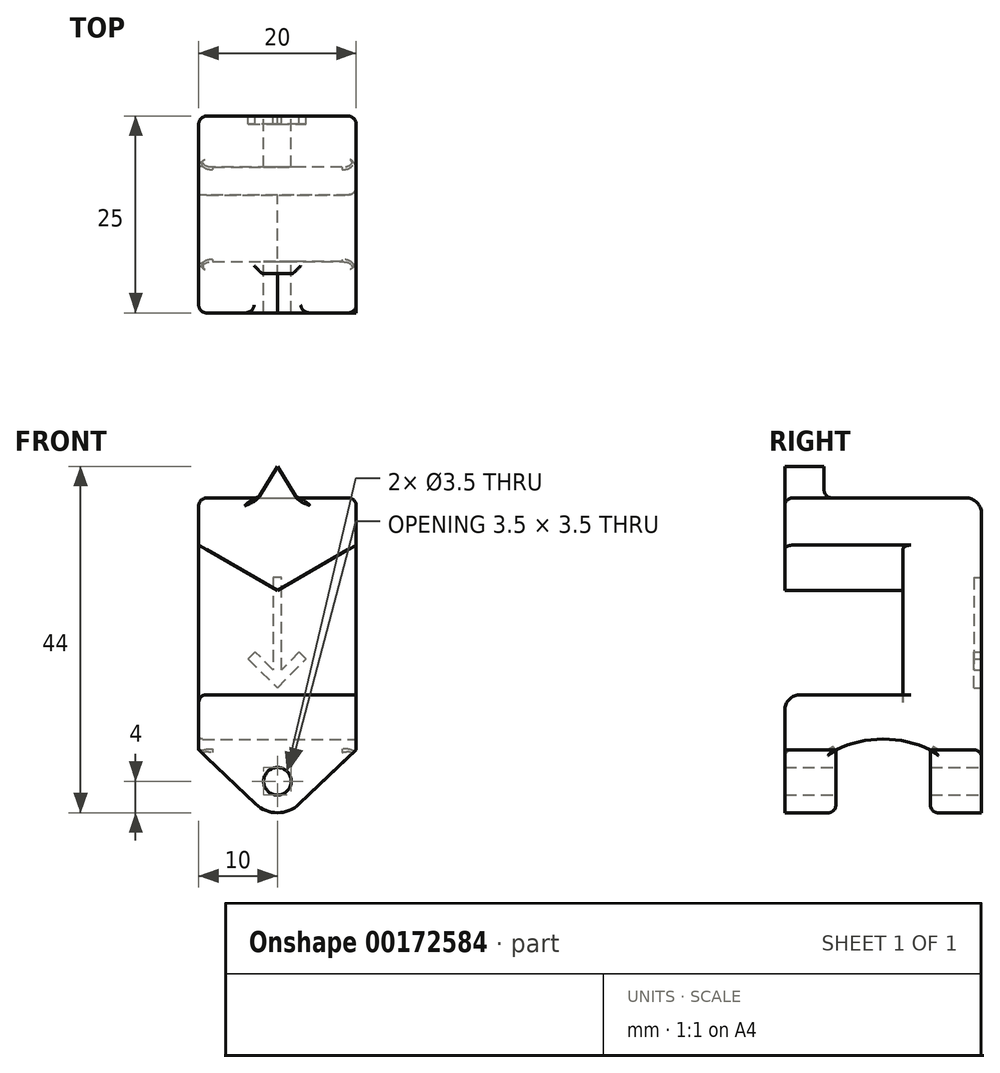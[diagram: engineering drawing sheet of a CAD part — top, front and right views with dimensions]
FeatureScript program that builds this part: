
annotation { "Feature Type Name" : "Feature", "Feature Type Description" : "" }
export const myFeature = defineFeature(function(context is Context, id is Id, definition is map)
    precondition{}
    {
        {
            var Q0;
            Q0=qCreatedBy(makeId("Front.planeOp"),FACE);
            var sketch = newSketch(context, id + "F0", { "sketchPlane" : qUnion([Q0])});
            skLineSegment(sketch, "E0.bottom", {"start": v(0, 0) * mm, "end": v(20, 0) * mm});
            skLineSegment(sketch, "E0.top", {"start": v(0, 40) * mm, "end": v(20, 40) * mm});
            skLineSegment(sketch, "E0.left", {"start": v(0, 0) * mm, "end": v(0, 40) * mm});
            skLineSegment(sketch, "E0.right", {"start": v(20, 0) * mm, "end": v(20, 40) * mm});
            skSolve(sketch);
        }
        {
            var Q0;
            Q0 = qSketchRegion(id + "F0", true);
            extrude(context, id + "F1", {"entities" : qUnion([Q0]), "depth" : 10 * mm});
        }
        {
            var Q0;
            Q0=makeQuery(id+"F1.opExtrude","CAP_FACE",FACE,{"disambiguationData":[OSD([sQuery(id+"F0.wireOp",EDGE,"E0.bottom"),sQuery(id+"F0.wireOp",EDGE,"E0.top"),sQuery(id+"F0.wireOp",EDGE,"E0.left"),sQuery(id+"F0.wireOp",EDGE,"E0.right")])],"isStart":false});
            var sketch = newSketch(context, id + "F2", { "sketchPlane" : qUnion([Q0])});
            skLineSegment(sketch, "E1", {"start": v(0, 40) * mm, "end": v(20, 40) * mm});
            skLineSegment(sketch, "E2", {"start": v(20, 40) * mm, "end": v(20, 34) * mm});
            skLineSegment(sketch, "E3", {"start": v(20, 34) * mm, "end": v(10, 28.23) * mm});
            skPoint(sketch, "E3.endSnap0", {"position": v(10, 40) * mm});
            skLineSegment(sketch, "E4", {"start": v(10, 28.23) * mm, "end": v(0, 34) * mm});
            skLineSegment(sketch, "E5", {"start": v(0, 34) * mm, "end": v(0, 40) * mm});
            skLineSegment(sketch, "E6.bottom", {"start": v(0, 0) * mm, "end": v(20, 0) * mm});
            skLineSegment(sketch, "E6.top", {"start": v(0, 15) * mm, "end": v(20, 15) * mm});
            skLineSegment(sketch, "E6.left", {"start": v(0, 0) * mm, "end": v(0, 15) * mm});
            skLineSegment(sketch, "E6.right", {"start": v(20, 0) * mm, "end": v(20, 15) * mm});
            skSolve(sketch);
        }
        {
            var Q0;
            Q0 = qSketchRegion(id + "F2", true);
            extrude(context, id + "F3", {"entities" : qUnion([Q0]), "operationType" : NewBodyOperationType.ADD, "depth" : 15 * mm});
        }
        {
            var Q0;
            Q0=makeQuery(id+"F3.boolean.opBoolean","MERGE",FACE,{"derivedFrom":[makeQuery(id+"F1.opExtrude","SWEPT_FACE",FACE,{"disambiguationData":[OSD([sQuery(id+"F0.wireOp",EDGE,"E0.right")])]}),makeQuery(id+"F3.opExtrude","SWEPT_FACE",FACE,{"disambiguationData":[OSD([sQuery(id+"F2.wireOp",EDGE,"E2")])]}),makeQuery(id+"F3.opExtrude","SWEPT_FACE",FACE,{"disambiguationData":[OSD([sQuery(id+"F2.wireOp",EDGE,"E6.right")])]})]});
            var sketch = newSketch(context, id + "F4", { "sketchPlane" : qUnion([Q0])});
            skLineSegment(sketch, "E7.bottom", {"start": v(-18.5, 0) * mm, "end": v(-6.5, 0) * mm});
            skLineSegment(sketch, "E7.top", {"start": v(-18.5, 8) * mm, "end": v(-6.5, 8) * mm});
            skLineSegment(sketch, "E7.left", {"start": v(-18.5, 0) * mm, "end": v(-18.5, 8) * mm});
            skLineSegment(sketch, "E7.right", {"start": v(-6.5, 0) * mm, "end": v(-6.5, 8) * mm});
            skArc(sketch, "E8", {"start": v(-6.5, 8) * mm, "mid": v(-12.5, 9.35) * mm, "end": v(-18.5, 8) * mm});
            skSolve(sketch);
        }
        {
            var Q0;
            Q0 = qSketchRegion(id + "F4", true);
            extrude(context, id + "F5", {"entities" : qUnion([Q0]), "operationType" : NewBodyOperationType.REMOVE, "oppositeDirection" : true, "depth" : 25 * mm});
        }
        {
            var Q0;
            Q0=makeQuery(id+"F5.boolean.opBoolean","COPY",FACE,{"derivedFrom":makeQuery(id+"F5.opExtrude","SWEPT_FACE",FACE,{"disambiguationData":[OSD([sQuery(id+"F4.wireOp",EDGE,"E7.left")])]})});
            var sketch = newSketch(context, id + "F6", { "sketchPlane" : qUnion([Q0])});
            skCircle(sketch, "E9", {"center": v(-10, 4) * mm, "radius": 1.75 * mm});
            skPoint(sketch, "E9.centerSnap0", {"position": v(-20, 4) * mm});
            skPoint(sketch, "E9.centerSnap1", {"position": v(-10, 0) * mm});
            skSolve(sketch);
        }
        {
            var Q0;
            Q0 = qSketchRegion(id + "F6", true);
            extrude(context, id + "F7", {"entities" : qUnion([Q0]), "operationType" : NewBodyOperationType.REMOVE, "oppositeDirection" : true, "depth" : 25 * mm, "hasSecondDirection" : true, "secondDirectionOppositeDirection" : false, "secondDirectionDepth" : 25 * mm});
        }
        {
            var Q0;
            Q0=makeQuery(id+"F3.opExtrude","CAP_FACE",FACE,{"disambiguationData":[OSD([sQuery(id+"F2.wireOp",EDGE,"E6.bottom"),sQuery(id+"F2.wireOp",EDGE,"E6.top"),sQuery(id+"F2.wireOp",EDGE,"E6.left"),sQuery(id+"F2.wireOp",EDGE,"E6.right")])],"isStart":false});
            var sketch = newSketch(context, id + "F8", { "sketchPlane" : qUnion([Q0])});
            skArc(sketch, "E10", {"start": v(10, 0) * mm, "mid": v(11.49, 0.29) * mm, "end": v(12.76, 1.1) * mm});
            skLineSegment(sketch, "E11", {"start": v(12.76, 1.1) * mm, "end": v(20, 8) * mm});
            skLineSegment(sketch, "E12", {"start": v(10, 4) * mm, "end": v(10, 0) * mm, "construction": true});
            skLineSegment(sketch, "E13.MirrorCS", {"start": v(7.24, 1.1) * mm, "end": v(0, 8) * mm});
            skArc(sketch, "E14.MirrorCS", {"start": v(10, 0) * mm, "mid": v(8.51, 0.29) * mm, "end": v(7.24, 1.1) * mm});
            skSolve(sketch);
        }
        {
            var Q0;
            {var subQ0=sQuery(id+"F8.wireOp",EDGE,"E10");Q0=makeQuery(id+"F8.imprint","IMPRINT",FACE,{"disambiguationData":[TD([[makeQuery(id+"F8.imprint","IMPRINT",EDGE,{"derivedFrom":subQ0}),-1.0]])]});}
            var Q1;
            {var subQ0=sQuery(id+"F8.wireOp",EDGE,"E13.MirrorCS");Q1=makeQuery(id+"F8.imprint","IMPRINT",FACE,{"disambiguationData":[TD([[makeQuery(id+"F8.imprint","IMPRINT",EDGE,{"derivedFrom":subQ0}),1.0]])]});}
            extrude(context, id + "F9", {"entities" : qUnion([Q0, Q1]), "operationType" : NewBodyOperationType.REMOVE, "oppositeDirection" : true, "depth" : 25 * mm});
        }
        {
            var Q0;
            Q0=makeQuery(id+"F1.opExtrude","CAP_EDGE",EDGE,{"disambiguationData":[OSD([sQuery(id+"F0.wireOp",EDGE,"E0.top")])],"isStart":true});
            var Q1;
            Q1=makeQuery(id+"F3.opExtrude","CAP_EDGE",EDGE,{"disambiguationData":[OSD([sQuery(id+"F2.wireOp",EDGE,"E6.top")])],"isStart":true});
            var Q2;
            Q2=makeQuery(id+"F3.opExtrude","CAP_EDGE",EDGE,{"disambiguationData":[OSD([sQuery(id+"F2.wireOp",EDGE,"E6.top")])],"isStart":false});
            fillet(context, id + "F10", {"entities" : qUnion([Q0, Q1, Q2]), "radius" : 2 * mm, "tangentPropagation" : true, "allowEdgeOverflow" : false});
        }
        {
            var Q0;
            Q0=makeQuery(id+"F1.opExtrude","CAP_EDGE",EDGE,{"disambiguationData":[OSD([sQuery(id+"F0.wireOp",EDGE,"E0.left")])],"isStart":true});
            var Q1;
            Q1=makeQuery(id+"F1.opExtrude","CAP_EDGE",EDGE,{"disambiguationData":[OSD([sQuery(id+"F0.wireOp",EDGE,"E0.right")])],"isStart":true});
            var Q2;
            Q2=makeQuery(id+"F9.boolean.opBoolean","COPY",EDGE,{"derivedFrom":makeQuery(id+"F9.opExtrude","CAP_EDGE",EDGE,{"disambiguationData":[OSD([sQuery(id+"F8.wireOp",EDGE,"E13.MirrorCS")])],"isStart":false})});
            var Q3;
            Q3=makeQuery(id+"F9.boolean.opBoolean","COPY",EDGE,{"derivedFrom":makeQuery(id+"F9.opExtrude","CAP_EDGE",EDGE,{"disambiguationData":[OSD([sQuery(id+"F8.wireOp",EDGE,"E13.MirrorCS")])],"isStart":true})});
            var Q4;
            Q4=makeQuery(id+"F9.boolean.opBoolean","INTERSECT",EDGE,{"derivedFrom":[makeQuery(id+"F5.boolean.opBoolean","COPY",FACE,{"derivedFrom":makeQuery(id+"F5.opExtrude","SWEPT_FACE",FACE,{"disambiguationData":[OSD([sQuery(id+"F4.wireOp",EDGE,"E7.right")])]})}),makeQuery(id+"F9.opExtrude","SWEPT_FACE",FACE,{"disambiguationData":[OSD([sQuery(id+"F8.wireOp",EDGE,"E13.MirrorCS")])]})]});
            var Q5;
            Q5=makeQuery(id+"F9.boolean.opBoolean","INTERSECT",EDGE,{"derivedFrom":[makeQuery(id+"F5.boolean.opBoolean","COPY",FACE,{"derivedFrom":makeQuery(id+"F5.opExtrude","SWEPT_FACE",FACE,{"disambiguationData":[OSD([sQuery(id+"F4.wireOp",EDGE,"E7.left")])]})}),makeQuery(id+"F9.opExtrude","SWEPT_FACE",FACE,{"disambiguationData":[OSD([sQuery(id+"F8.wireOp",EDGE,"E13.MirrorCS")])]})]});
            var Q6;
            Q6=makeQuery(id+"F3.opExtrude","SWEPT_EDGE",EDGE,{"disambiguationData":[OSD([sQuery(id+"F0.wireOp",EDGE,"E0.left"),sQuery(id+"F2.wireOp",EDGE,"E6.top"),sQuery(id+"F2.wireOp",EDGE,"E6.left")])]});
            var Q7;
            Q7=makeQuery(id+"F1.opExtrude","CAP_EDGE",EDGE,{"disambiguationData":[OSD([sQuery(id+"F0.wireOp",EDGE,"E0.right")])],"isStart":false});
            var Q8;
            Q8=makeQuery(id+"F3.opExtrude","CAP_EDGE",EDGE,{"disambiguationData":[OSD([sQuery(id+"F2.wireOp",EDGE,"E5")])],"isStart":false});
            var Q9;
            Q9=makeQuery(id+"F3.opExtrude","CAP_EDGE",EDGE,{"disambiguationData":[OSD([sQuery(id+"F2.wireOp",EDGE,"E1")])],"isStart":false});
            var Q10;
            Q10=makeQuery(id+"F3.opExtrude","CAP_EDGE",EDGE,{"disambiguationData":[OSD([sQuery(id+"F2.wireOp",EDGE,"E2")])],"isStart":false});
            fillet(context, id + "F11", {"entities" : qUnion([Q0, Q1, Q2, Q3, Q4, Q5, Q6, Q7, Q8, Q9, Q10]), "radius" : 1 * mm, "tangentPropagation" : true, "allowEdgeOverflow" : false});
        }
        {
            var Q0;
            Q0=makeQuery(id+"F5.boolean.opBoolean","COPY",EDGE,{"derivedFrom":makeQuery(id+"F5.opExtrude","SWEPT_EDGE",EDGE,{"disambiguationData":[OSD([sQuery(id+"F4.wireOp",EDGE,"E7.top"),sQuery(id+"F4.wireOp",EDGE,"E7.right")])]})});
            var Q1;
            Q1=makeQuery(id+"F5.boolean.opBoolean","COPY",EDGE,{"derivedFrom":makeQuery(id+"F5.opExtrude","SWEPT_EDGE",EDGE,{"disambiguationData":[OSD([sQuery(id+"F4.wireOp",EDGE,"E7.top"),sQuery(id+"F4.wireOp",EDGE,"E7.left")])]})});
            fillet(context, id + "F12", {"entities" : qUnion([Q0, Q1]), "radius" : 0.5 * mm, "tangentPropagation" : true, "allowEdgeOverflow" : false});
        }
        {
            var Q0;
            Q0=makeQuery(id+"F1.opExtrude","CAP_FACE",FACE,{"disambiguationData":[OSD([sQuery(id+"F0.wireOp",EDGE,"E0.bottom"),sQuery(id+"F0.wireOp",EDGE,"E0.top"),sQuery(id+"F0.wireOp",EDGE,"E0.left"),sQuery(id+"F0.wireOp",EDGE,"E0.right")])],"isStart":true});
            var sketch = newSketch(context, id + "F13", { "sketchPlane" : qUnion([Q0])});
            skLineSegment(sketch, "E15", {"start": v(-9.46, 29.87) * mm, "end": v(-9.46, 18.15) * mm});
            skLineSegment(sketch, "E16", {"start": v(-9.46, 18.15) * mm, "end": v(-7.17, 20.42) * mm});
            skLineSegment(sketch, "E17", {"start": v(-7.17, 20.42) * mm, "end": v(-6.3, 19.54) * mm});
            skLineSegment(sketch, "E18", {"start": v(-6.3, 19.54) * mm, "end": v(-10, 15.87) * mm});
            skLineSegment(sketch, "E19", {"start": v(-10, 15.87) * mm, "end": v(-13.65, 19.54) * mm});
            skLineSegment(sketch, "E20", {"start": v(-13.65, 19.54) * mm, "end": v(-12.76, 20.42) * mm});
            skLineSegment(sketch, "E21", {"start": v(-12.76, 20.42) * mm, "end": v(-10.51, 18.15) * mm});
            skLineSegment(sketch, "E22", {"start": v(-10.51, 18.15) * mm, "end": v(-10.51, 29.87) * mm});
            skLineSegment(sketch, "E23", {"start": v(-10.51, 29.87) * mm, "end": v(-9.46, 29.87) * mm});
            skSolve(sketch);
        }
        {
            var Q0;
            Q0 = qSketchRegion(id + "F13", true);
            extrude(context, id + "F14", {"entities" : qUnion([Q0]), "operationType" : NewBodyOperationType.REMOVE, "oppositeDirection" : true, "depth" : 1 * mm});
        }
        {
            var Q0;
            Q0=makeQuery(id+"F3.opExtrude","CAP_FACE",FACE,{"disambiguationData":[OSD([sQuery(id+"F2.wireOp",EDGE,"E1"),sQuery(id+"F2.wireOp",EDGE,"E2"),sQuery(id+"F2.wireOp",EDGE,"E3"),sQuery(id+"F2.wireOp",EDGE,"E4"),sQuery(id+"F2.wireOp",EDGE,"E5")])],"isStart":false});
            var sketch = newSketch(context, id + "F15", { "sketchPlane" : qUnion([Q0])});
            skLineSegment(sketch, "E24", {"start": v(10, 39) * mm, "end": v(13, 39) * mm});
            skLineSegment(sketch, "E25", {"start": v(13, 39) * mm, "end": v(10, 44) * mm});
            skLineSegment(sketch, "E26", {"start": v(10, 44) * mm, "end": v(7, 39) * mm});
            skLineSegment(sketch, "E27", {"start": v(7, 39) * mm, "end": v(10, 39) * mm});
            skSolve(sketch);
        }
        {
            var Q0;
            Q0 = qSketchRegion(id + "F15", true);
            extrude(context, id + "F16", {"entities" : qUnion([Q0]), "operationType" : NewBodyOperationType.ADD, "oppositeDirection" : true, "depth" : 5 * mm});
        }
        {
            var Q0;
            Q0=makeQuery(id+"F16.boolean.opBoolean","INTERSECT",EDGE,{"derivedFrom":[makeQuery(id+"F3.boolean.opBoolean","MERGE",FACE,{"derivedFrom":[makeQuery(id+"F1.opExtrude","SWEPT_FACE",FACE,{"disambiguationData":[OSD([sQuery(id+"F0.wireOp",EDGE,"E0.top")])]}),makeQuery(id+"F3.opExtrude","SWEPT_FACE",FACE,{"disambiguationData":[OSD([sQuery(id+"F2.wireOp",EDGE,"E1")])]})]}),makeQuery(id+"F16.opExtrude","SWEPT_FACE",FACE,{"disambiguationData":[OSD([sQuery(id+"F15.wireOp",EDGE,"E26")])]})]});
            var Q1;
            Q1=makeQuery(id+"F16.boolean.opBoolean","INTERSECT",EDGE,{"derivedFrom":[makeQuery(id+"F3.boolean.opBoolean","MERGE",FACE,{"derivedFrom":[makeQuery(id+"F1.opExtrude","SWEPT_FACE",FACE,{"disambiguationData":[OSD([sQuery(id+"F0.wireOp",EDGE,"E0.top")])]}),makeQuery(id+"F3.opExtrude","SWEPT_FACE",FACE,{"disambiguationData":[OSD([sQuery(id+"F2.wireOp",EDGE,"E1")])]})]}),makeQuery(id+"F16.opExtrude","SWEPT_FACE",FACE,{"disambiguationData":[OSD([sQuery(id+"F15.wireOp",EDGE,"E25")])]})]});
            var Q2;
            Q2=makeQuery(id+"F16.boolean.opBoolean","INTERSECT",EDGE,{"derivedFrom":[makeQuery(id+"F3.boolean.opBoolean","MERGE",FACE,{"derivedFrom":[makeQuery(id+"F1.opExtrude","SWEPT_FACE",FACE,{"disambiguationData":[OSD([sQuery(id+"F0.wireOp",EDGE,"E0.top")])]}),makeQuery(id+"F3.opExtrude","SWEPT_FACE",FACE,{"disambiguationData":[OSD([sQuery(id+"F2.wireOp",EDGE,"E1")])]})]}),makeQuery(id+"F16.opExtrude","CAP_FACE",FACE,{"disambiguationData":[OSD([sQuery(id+"F15.wireOp",EDGE,"E24"),sQuery(id+"F15.wireOp",EDGE,"E25"),sQuery(id+"F15.wireOp",EDGE,"E26"),sQuery(id+"F15.wireOp",EDGE,"E27")])],"isStart":false})]});
            fillet(context, id + "F17", {"entities" : qUnion([Q0, Q1, Q2]), "radius" : 1 * mm, "tangentPropagation" : true, "allowEdgeOverflow" : false});
        }
        {
            var Q0;
            Q0=makeQuery(id+"F5.boolean.opBoolean","COPY",EDGE,{"derivedFrom":makeQuery(id+"F5.opExtrude","CAP_EDGE",EDGE,{"disambiguationData":[OSD([sQuery(id+"F4.wireOp",EDGE,"E8")])],"isStart":true})});
            var Q1;
            Q1=makeQuery(id+"F5.boolean.opBoolean","INTERSECT",EDGE,{"derivedFrom":[makeQuery(id+"F3.boolean.opBoolean","MERGE",FACE,{"derivedFrom":[makeQuery(id+"F1.opExtrude","SWEPT_FACE",FACE,{"disambiguationData":[OSD([sQuery(id+"F0.wireOp",EDGE,"E0.left")])]}),makeQuery(id+"F3.opExtrude","SWEPT_FACE",FACE,{"disambiguationData":[OSD([sQuery(id+"F2.wireOp",EDGE,"E5")])]}),makeQuery(id+"F3.opExtrude","SWEPT_FACE",FACE,{"disambiguationData":[OSD([sQuery(id+"F2.wireOp",EDGE,"E6.left")])]})]}),makeQuery(id+"F5.opExtrude","SWEPT_FACE",FACE,{"disambiguationData":[OSD([sQuery(id+"F4.wireOp",EDGE,"E8")])]})]});
            fillet(context, id + "F18", {"entities" : qUnion([Q0, Q1]), "radius" : 0.5 * mm, "tangentPropagation" : true, "allowEdgeOverflow" : false});
        }
    });
